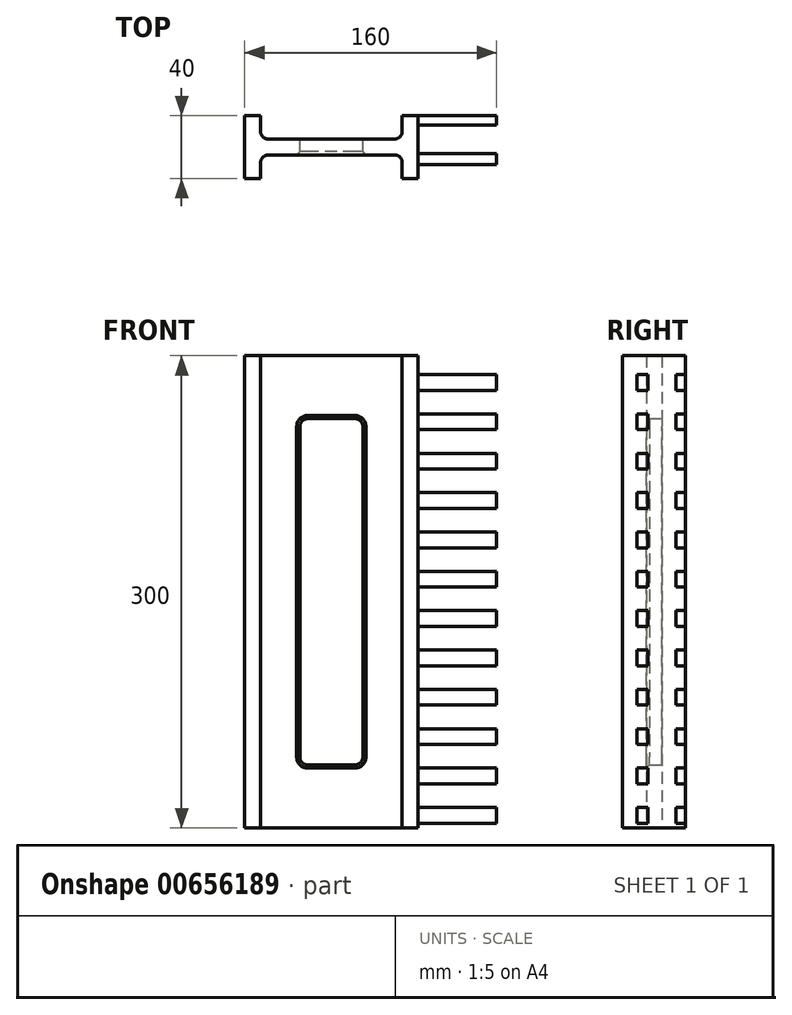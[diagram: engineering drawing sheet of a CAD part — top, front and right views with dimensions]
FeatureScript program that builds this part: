
annotation { "Feature Type Name" : "Feature", "Feature Type Description" : "" }
export const myFeature = defineFeature(function(context is Context, id is Id, definition is map)
    precondition{}
    {
        {
            var Q0;
            Q0=qCreatedBy(makeId("Top.planeOp"),FACE);
            var sketch = newSketch(context, id + "F0", { "sketchPlane" : qUnion([Q0])});
            skLineSegment(sketch, "E0.bottom", {"start": v(0, -5) * mm, "end": v(-40, -5) * mm});
            skLineSegment(sketch, "E0.top", {"start": v(0, 5) * mm, "end": v(-40, 5) * mm});
            skPoint(sketch, "E0.middle", {"position": v(0, 0) * mm});
            skLineSegment(sketch, "E1.bottom", {"start": v(-45, -20) * mm, "end": v(-55, -20) * mm});
            skLineSegment(sketch, "E1.top", {"start": v(-45, 20) * mm, "end": v(-55, 20) * mm});
            skLineSegment(sketch, "E1.left", {"start": v(-45, 10) * mm, "end": v(-45, 20) * mm});
            skLineSegment(sketch, "E1.right", {"start": v(-55, -20) * mm, "end": v(-55, 20) * mm});
            skPoint(sketch, "E1.middle", {"position": v(-50, 0) * mm});
            skPoint(sketch, "E2.orphan", {"position": v(-50, 5) * mm});
            skPoint(sketch, "E0.right.start.orphan", {"position": v(-50, -5) * mm});
            skArc(sketch, "E3.filletArc", {"start": v(-45, 10) * mm, "mid": v(-43.54, 6.46) * mm, "end": v(-40, 5) * mm});
            skLineSegment(sketch, "E4", {"start": v(-45, -20) * mm, "end": v(-45, -10) * mm});
            skPoint(sketch, "E5.visualSharp", {"position": v(-45, -5) * mm});
            skArc(sketch, "E5.filletArc", {"start": v(-40, -5) * mm, "mid": v(-43.54, -6.46) * mm, "end": v(-45, -10) * mm});
            skLineSegment(sketch, "E6", {"start": v(0, 54.25) * mm, "end": v(0, -61.34) * mm, "construction": true});
            skPoint(sketch, "E0.left.end.orphan", {"position": v(50, 5) * mm});
            skPoint(sketch, "E0.left.start.orphan", {"position": v(50, -5) * mm});
            skLineSegment(sketch, "E7.MirrorCS", {"start": v(-45, 30) * mm, "end": v(-45, 20) * mm});
            skLineSegment(sketch, "E8.MirrorCS", {"start": v(0, 5) * mm, "end": v(40, 5) * mm});
            skArc(sketch, "E9.MirrorCS", {"start": v(45, 10) * mm, "mid": v(43.54, 6.46) * mm, "end": v(40, 5) * mm});
            skLineSegment(sketch, "E10.MirrorCS", {"start": v(45, 10) * mm, "end": v(45, 20) * mm});
            skLineSegment(sketch, "E11.MirrorCS", {"start": v(45, 20) * mm, "end": v(55, 20) * mm});
            skLineSegment(sketch, "E12.MirrorCS", {"start": v(55, -20) * mm, "end": v(55, 20) * mm});
            skLineSegment(sketch, "E13.MirrorCS", {"start": v(45, -20) * mm, "end": v(55, -20) * mm});
            skLineSegment(sketch, "E14.MirrorCS", {"start": v(45, -20) * mm, "end": v(45, -10) * mm});
            skArc(sketch, "E15.MirrorCS", {"start": v(40, -5) * mm, "mid": v(43.54, -6.46) * mm, "end": v(45, -10) * mm});
            skLineSegment(sketch, "E16.MirrorCS", {"start": v(0, -5) * mm, "end": v(40, -5) * mm});
            skSolve(sketch);
        }
        {
            var Q0;
            Q0=makeQuery(id+"F0.imprint","IMPRINT",FACE,{"disambiguationData":[TD([[makeQuery(id+"F0.imprint","IMPRINT",EDGE,{"derivedFrom":sQuery(id+"F0.wireOp",EDGE,"E0.bottom")}),-1.0]])]});
            extrude(context, id + "F1", {"entities" : qUnion([Q0]), "depth" : 300 * mm, "offsetDistance" : 25 * mm});
        }
        {
            var Q0;
            Q0=makeQuery(id+"F1.opExtrude","SWEPT_FACE",FACE,{"disambiguationData":[OSD([sQuery(id+"F0.wireOp",EDGE,"E0.top"),sQuery(id+"F0.wireOp",EDGE,"E8.MirrorCS")])]});
            var sketch = newSketch(context, id + "F2", { "sketchPlane" : qUnion([Q0])});
            skLineSegment(sketch, "E17.bottom", {"start": v(-15, 40) * mm, "end": v(15, 40) * mm});
            skLineSegment(sketch, "E17.top", {"start": v(-15, 260) * mm, "end": v(15, 260) * mm});
            skLineSegment(sketch, "E17.left", {"start": v(-20, 45) * mm, "end": v(-20, 255) * mm});
            skLineSegment(sketch, "E17.right", {"start": v(20, 45) * mm, "end": v(20, 255) * mm});
            skPoint(sketch, "E17.middle", {"position": v(0, 150) * mm});
            skPoint(sketch, "E18.visualSharp", {"position": v(20, 260) * mm});
            skArc(sketch, "E18.filletArc", {"start": v(20, 255) * mm, "mid": v(18.54, 258.54) * mm, "end": v(15, 260) * mm});
            skPoint(sketch, "E19.visualSharp", {"position": v(-20, 260) * mm});
            skArc(sketch, "E19.filletArc", {"start": v(-15, 260) * mm, "mid": v(-18.54, 258.54) * mm, "end": v(-20, 255) * mm});
            skPoint(sketch, "E20.visualSharp", {"position": v(20, 40) * mm});
            skArc(sketch, "E20.filletArc", {"start": v(15, 40) * mm, "mid": v(18.54, 41.46) * mm, "end": v(20, 45) * mm});
            skPoint(sketch, "E21.visualSharp", {"position": v(-20, 40) * mm});
            skArc(sketch, "E21.filletArc", {"start": v(-20, 45) * mm, "mid": v(-18.54, 41.46) * mm, "end": v(-15, 40) * mm});
            skSolve(sketch);
        }
        {
            var Q0;
            Q0 = qSketchRegion(id + "F2", true);
            extrude(context, id + "F3", {"entities" : qUnion([Q0]), "operationType" : NewBodyOperationType.REMOVE, "oppositeDirection" : true, "depth" : 25 * mm, "offsetDistance" : 25 * mm});
        }
        {
            var Q0;
            Q0=makeQuery(id+"F3.boolean.opBoolean","INTERSECT",EDGE,{"derivedFrom":[makeQuery(id+"F1.opExtrude","SWEPT_FACE",FACE,{"disambiguationData":[OSD([sQuery(id+"F0.wireOp",EDGE,"E0.bottom"),sQuery(id+"F0.wireOp",EDGE,"E16.MirrorCS")])]}),makeQuery(id+"F3.opExtrude","SWEPT_FACE",FACE,{"disambiguationData":[OSD([sQuery(id+"F2.wireOp",EDGE,"E17.top")])]})]});
            chamfer(context, id + "F4", {"entities" : qUnion([Q0]), "width" : 2 * mm, "tangentPropagation" : true});
        }
        {
            var Q0;
            Q0=makeQuery(id+"F1.opExtrude","SWEPT_FACE",FACE,{"disambiguationData":[OSD([sQuery(id+"F0.wireOp",EDGE,"E12.MirrorCS")])]});
            var sketch = newSketch(context, id + "F5", { "sketchPlane" : qUnion([Q0])});
            skLineSegment(sketch, "E22.bottom", {"start": v(-4, 3) * mm, "end": v(-11, 3) * mm});
            skLineSegment(sketch, "E22.top", {"start": v(-4, 13) * mm, "end": v(-11, 13) * mm});
            skLineSegment(sketch, "E22.left", {"start": v(-4, 3) * mm, "end": v(-4, 13) * mm});
            skPoint(sketch, "E22.middle", {"position": v(-20, 8) * mm});
            skLineSegment(sketch, "E23.0.1.0", {"start": v(-4, 38) * mm, "end": v(-11, 38) * mm});
            skLineSegment(sketch, "E23.0.1.1", {"start": v(-4, 28) * mm, "end": v(-4, 38) * mm});
            skLineSegment(sketch, "E23.0.1.2", {"start": v(-4, 28) * mm, "end": v(-11, 28) * mm});
            skLineSegment(sketch, "E23.0.1.3", {"start": v(-36, 28) * mm, "end": v(-36, 38) * mm});
            skLineSegment(sketch, "E23.0.2.0", {"start": v(-4, 63) * mm, "end": v(-11, 63) * mm});
            skLineSegment(sketch, "E23.0.2.1", {"start": v(-4, 53) * mm, "end": v(-4, 63) * mm});
            skLineSegment(sketch, "E23.0.2.2", {"start": v(-4, 53) * mm, "end": v(-11, 53) * mm});
            skLineSegment(sketch, "E23.0.3.0", {"start": v(-4, 88) * mm, "end": v(-11, 88) * mm});
            skLineSegment(sketch, "E23.0.3.1", {"start": v(-4, 78) * mm, "end": v(-4, 88) * mm});
            skLineSegment(sketch, "E23.0.3.2", {"start": v(-4, 78) * mm, "end": v(-11, 78) * mm});
            skLineSegment(sketch, "E23.0.4.0", {"start": v(-4, 113) * mm, "end": v(-11, 113) * mm});
            skLineSegment(sketch, "E23.0.4.1", {"start": v(-4, 103) * mm, "end": v(-4, 113) * mm});
            skLineSegment(sketch, "E23.0.4.2", {"start": v(-4, 103) * mm, "end": v(-11, 103) * mm});
            skLineSegment(sketch, "E23.0.5.0", {"start": v(-4, 138) * mm, "end": v(-11, 138) * mm});
            skLineSegment(sketch, "E23.0.5.1", {"start": v(-4, 128) * mm, "end": v(-4, 138) * mm});
            skLineSegment(sketch, "E23.0.5.2", {"start": v(-4, 128) * mm, "end": v(-11, 128) * mm});
            skLineSegment(sketch, "E23.0.6.0", {"start": v(-4, 163) * mm, "end": v(-11, 163) * mm});
            skLineSegment(sketch, "E23.0.6.1", {"start": v(-4, 153) * mm, "end": v(-4, 163) * mm});
            skLineSegment(sketch, "E23.0.6.2", {"start": v(-4, 153) * mm, "end": v(-11, 153) * mm});
            skLineSegment(sketch, "E23.0.7.0", {"start": v(-4, 188) * mm, "end": v(-11, 188) * mm});
            skLineSegment(sketch, "E23.0.7.1", {"start": v(-4, 178) * mm, "end": v(-4, 188) * mm});
            skLineSegment(sketch, "E23.0.7.2", {"start": v(-4, 178) * mm, "end": v(-11, 178) * mm});
            skLineSegment(sketch, "E23.0.8.0", {"start": v(-4, 213) * mm, "end": v(-11, 213) * mm});
            skLineSegment(sketch, "E23.0.8.1", {"start": v(-4, 203) * mm, "end": v(-4, 213) * mm});
            skLineSegment(sketch, "E23.0.8.2", {"start": v(-4, 203) * mm, "end": v(-11, 203) * mm});
            skLineSegment(sketch, "E23.0.9.0", {"start": v(-4, 238) * mm, "end": v(-11, 238) * mm});
            skLineSegment(sketch, "E23.0.9.1", {"start": v(-4, 228) * mm, "end": v(-4, 238) * mm});
            skLineSegment(sketch, "E23.0.9.2", {"start": v(-4, 228) * mm, "end": v(-11, 228) * mm});
            skLineSegment(sketch, "E23.0.10.0", {"start": v(-4, 263) * mm, "end": v(-11, 263) * mm});
            skLineSegment(sketch, "E23.0.10.1", {"start": v(-4, 253) * mm, "end": v(-4, 263) * mm});
            skLineSegment(sketch, "E23.0.10.2", {"start": v(-4, 253) * mm, "end": v(-11, 253) * mm});
            skLineSegment(sketch, "E23.0.11.0", {"start": v(-4, 288) * mm, "end": v(-11, 288) * mm});
            skLineSegment(sketch, "E23.0.11.1", {"start": v(-4, 278) * mm, "end": v(-4, 288) * mm});
            skLineSegment(sketch, "E23.0.11.2", {"start": v(-4, 278) * mm, "end": v(-11, 278) * mm});
            skLineSegment(sketch, "E23.1.0.0", {"start": v(21, 13) * mm, "end": v(14, 13) * mm});
            skLineSegment(sketch, "E23.1.0.1", {"start": v(21, 3) * mm, "end": v(21, 13) * mm});
            skLineSegment(sketch, "E23.1.0.2", {"start": v(21, 3) * mm, "end": v(14, 3) * mm});
            skLineSegment(sketch, "E23.1.0.3", {"start": v(-11, 3) * mm, "end": v(-11, 13) * mm});
            skLineSegment(sketch, "E23.1.1.0", {"start": v(21, 38) * mm, "end": v(14, 38) * mm});
            skLineSegment(sketch, "E23.1.1.1", {"start": v(21, 28) * mm, "end": v(21, 38) * mm});
            skLineSegment(sketch, "E23.1.1.2", {"start": v(21, 28) * mm, "end": v(14, 28) * mm});
            skLineSegment(sketch, "E23.1.1.3", {"start": v(-11, 28) * mm, "end": v(-11, 38) * mm});
            skLineSegment(sketch, "E23.1.2.0", {"start": v(21, 63) * mm, "end": v(14, 63) * mm});
            skLineSegment(sketch, "E23.1.2.1", {"start": v(21, 53) * mm, "end": v(21, 63) * mm});
            skLineSegment(sketch, "E23.1.2.2", {"start": v(21, 53) * mm, "end": v(14, 53) * mm});
            skLineSegment(sketch, "E23.1.2.3", {"start": v(-11, 53) * mm, "end": v(-11, 63) * mm});
            skLineSegment(sketch, "E23.1.3.0", {"start": v(21, 88) * mm, "end": v(14, 88) * mm});
            skLineSegment(sketch, "E23.1.3.1", {"start": v(21, 78) * mm, "end": v(21, 88) * mm});
            skLineSegment(sketch, "E23.1.3.2", {"start": v(21, 78) * mm, "end": v(14, 78) * mm});
            skLineSegment(sketch, "E23.1.3.3", {"start": v(-11, 78) * mm, "end": v(-11, 88) * mm});
            skLineSegment(sketch, "E23.1.4.0", {"start": v(21, 113) * mm, "end": v(14, 113) * mm});
            skLineSegment(sketch, "E23.1.4.1", {"start": v(21, 103) * mm, "end": v(21, 113) * mm});
            skLineSegment(sketch, "E23.1.4.2", {"start": v(21, 103) * mm, "end": v(14, 103) * mm});
            skLineSegment(sketch, "E23.1.4.3", {"start": v(-11, 103) * mm, "end": v(-11, 113) * mm});
            skLineSegment(sketch, "E23.1.5.0", {"start": v(21, 138) * mm, "end": v(14, 138) * mm});
            skLineSegment(sketch, "E23.1.5.1", {"start": v(21, 128) * mm, "end": v(21, 138) * mm});
            skLineSegment(sketch, "E23.1.5.2", {"start": v(21, 128) * mm, "end": v(14, 128) * mm});
            skLineSegment(sketch, "E23.1.5.3", {"start": v(-11, 128) * mm, "end": v(-11, 138) * mm});
            skLineSegment(sketch, "E23.1.6.0", {"start": v(21, 163) * mm, "end": v(14, 163) * mm});
            skLineSegment(sketch, "E23.1.6.1", {"start": v(21, 153) * mm, "end": v(21, 163) * mm});
            skLineSegment(sketch, "E23.1.6.2", {"start": v(21, 153) * mm, "end": v(14, 153) * mm});
            skLineSegment(sketch, "E23.1.6.3", {"start": v(-11, 153) * mm, "end": v(-11, 163) * mm});
            skLineSegment(sketch, "E23.1.7.0", {"start": v(21, 188) * mm, "end": v(14, 188) * mm});
            skLineSegment(sketch, "E23.1.7.1", {"start": v(21, 178) * mm, "end": v(21, 188) * mm});
            skLineSegment(sketch, "E23.1.7.2", {"start": v(21, 178) * mm, "end": v(14, 178) * mm});
            skLineSegment(sketch, "E23.1.7.3", {"start": v(-11, 178) * mm, "end": v(-11, 188) * mm});
            skLineSegment(sketch, "E23.1.8.0", {"start": v(21, 213) * mm, "end": v(14, 213) * mm});
            skLineSegment(sketch, "E23.1.8.1", {"start": v(21, 203) * mm, "end": v(21, 213) * mm});
            skLineSegment(sketch, "E23.1.8.2", {"start": v(21, 203) * mm, "end": v(14, 203) * mm});
            skLineSegment(sketch, "E23.1.8.3", {"start": v(-11, 203) * mm, "end": v(-11, 213) * mm});
            skLineSegment(sketch, "E23.1.9.0", {"start": v(21, 238) * mm, "end": v(14, 238) * mm});
            skLineSegment(sketch, "E23.1.9.1", {"start": v(21, 228) * mm, "end": v(21, 238) * mm});
            skLineSegment(sketch, "E23.1.9.2", {"start": v(21, 228) * mm, "end": v(14, 228) * mm});
            skLineSegment(sketch, "E23.1.9.3", {"start": v(-11, 228) * mm, "end": v(-11, 238) * mm});
            skLineSegment(sketch, "E23.1.10.0", {"start": v(21, 263) * mm, "end": v(14, 263) * mm});
            skLineSegment(sketch, "E23.1.10.1", {"start": v(21, 253) * mm, "end": v(21, 263) * mm});
            skLineSegment(sketch, "E23.1.10.2", {"start": v(21, 253) * mm, "end": v(14, 253) * mm});
            skLineSegment(sketch, "E23.1.10.3", {"start": v(-11, 253) * mm, "end": v(-11, 263) * mm});
            skLineSegment(sketch, "E23.1.11.0", {"start": v(21, 288) * mm, "end": v(14, 288) * mm});
            skLineSegment(sketch, "E23.1.11.1", {"start": v(21, 278) * mm, "end": v(21, 288) * mm});
            skLineSegment(sketch, "E23.1.11.2", {"start": v(21, 278) * mm, "end": v(14, 278) * mm});
            skLineSegment(sketch, "E23.1.11.3", {"start": v(-11, 278) * mm, "end": v(-11, 288) * mm});
            skLineSegment(sketch, "E23.2.0.0", {"start": v(21, 13) * mm, "end": v(14, 13) * mm});
            skLineSegment(sketch, "E23.2.0.2", {"start": v(21, 3) * mm, "end": v(14, 3) * mm});
            skLineSegment(sketch, "E23.2.0.3", {"start": v(14, 3) * mm, "end": v(14, 13) * mm});
            skLineSegment(sketch, "E23.2.1.0", {"start": v(21, 38) * mm, "end": v(14, 38) * mm});
            skLineSegment(sketch, "E23.2.1.2", {"start": v(21, 28) * mm, "end": v(14, 28) * mm});
            skLineSegment(sketch, "E23.2.1.3", {"start": v(14, 28) * mm, "end": v(14, 38) * mm});
            skLineSegment(sketch, "E23.2.2.0", {"start": v(21, 63) * mm, "end": v(14, 63) * mm});
            skLineSegment(sketch, "E23.2.2.2", {"start": v(21, 53) * mm, "end": v(14, 53) * mm});
            skLineSegment(sketch, "E23.2.2.3", {"start": v(14, 53) * mm, "end": v(14, 63) * mm});
            skLineSegment(sketch, "E23.2.3.0", {"start": v(21, 88) * mm, "end": v(14, 88) * mm});
            skLineSegment(sketch, "E23.2.3.2", {"start": v(21, 78) * mm, "end": v(14, 78) * mm});
            skLineSegment(sketch, "E23.2.3.3", {"start": v(14, 78) * mm, "end": v(14, 88) * mm});
            skLineSegment(sketch, "E23.2.4.0", {"start": v(21, 113) * mm, "end": v(14, 113) * mm});
            skLineSegment(sketch, "E23.2.4.2", {"start": v(21, 103) * mm, "end": v(14, 103) * mm});
            skLineSegment(sketch, "E23.2.4.3", {"start": v(14, 103) * mm, "end": v(14, 113) * mm});
            skLineSegment(sketch, "E23.2.5.0", {"start": v(21, 138) * mm, "end": v(14, 138) * mm});
            skLineSegment(sketch, "E23.2.5.2", {"start": v(21, 128) * mm, "end": v(14, 128) * mm});
            skLineSegment(sketch, "E23.2.5.3", {"start": v(14, 128) * mm, "end": v(14, 138) * mm});
            skLineSegment(sketch, "E23.2.6.0", {"start": v(21, 163) * mm, "end": v(14, 163) * mm});
            skLineSegment(sketch, "E23.2.6.2", {"start": v(21, 153) * mm, "end": v(14, 153) * mm});
            skLineSegment(sketch, "E23.2.6.3", {"start": v(14, 153) * mm, "end": v(14, 163) * mm});
            skLineSegment(sketch, "E23.2.7.0", {"start": v(21, 188) * mm, "end": v(14, 188) * mm});
            skLineSegment(sketch, "E23.2.7.2", {"start": v(21, 178) * mm, "end": v(14, 178) * mm});
            skLineSegment(sketch, "E23.2.7.3", {"start": v(14, 178) * mm, "end": v(14, 188) * mm});
            skLineSegment(sketch, "E23.2.8.0", {"start": v(21, 213) * mm, "end": v(14, 213) * mm});
            skLineSegment(sketch, "E23.2.8.2", {"start": v(21, 203) * mm, "end": v(14, 203) * mm});
            skLineSegment(sketch, "E23.2.8.3", {"start": v(14, 203) * mm, "end": v(14, 213) * mm});
            skLineSegment(sketch, "E23.2.9.0", {"start": v(21, 238) * mm, "end": v(14, 238) * mm});
            skLineSegment(sketch, "E23.2.9.2", {"start": v(21, 228) * mm, "end": v(14, 228) * mm});
            skLineSegment(sketch, "E23.2.9.3", {"start": v(14, 228) * mm, "end": v(14, 238) * mm});
            skLineSegment(sketch, "E23.2.10.0", {"start": v(21, 263) * mm, "end": v(14, 263) * mm});
            skLineSegment(sketch, "E23.2.10.2", {"start": v(21, 253) * mm, "end": v(14, 253) * mm});
            skLineSegment(sketch, "E23.2.10.3", {"start": v(14, 253) * mm, "end": v(14, 263) * mm});
            skLineSegment(sketch, "E23.2.11.0", {"start": v(21, 288) * mm, "end": v(14, 288) * mm});
            skLineSegment(sketch, "E23.2.11.2", {"start": v(21, 278) * mm, "end": v(14, 278) * mm});
            skLineSegment(sketch, "E23.2.11.3", {"start": v(14, 278) * mm, "end": v(14, 288) * mm});
            skLineSegment(sketch, "E23.direction2", {"start": v(-36, 13) * mm, "end": v(-36, 38) * mm, "construction": true});
            skPoint(sketch, "E24.orphan", {"position": v(46, 278) * mm});
            skPoint(sketch, "E25.orphan", {"position": v(46, 263) * mm});
            skPoint(sketch, "E26.orphan", {"position": v(46, 253) * mm});
            skPoint(sketch, "E27.orphan", {"position": v(46, 238) * mm});
            skPoint(sketch, "E28.orphan", {"position": v(46, 228) * mm});
            skPoint(sketch, "E29.orphan", {"position": v(46, 203) * mm});
            skPoint(sketch, "E30.orphan", {"position": v(46, 178) * mm});
            skPoint(sketch, "E31.orphan", {"position": v(46, 188) * mm});
            skPoint(sketch, "E32.orphan", {"position": v(46, 153) * mm});
            skPoint(sketch, "E33.orphan", {"position": v(46, 128) * mm});
            skPoint(sketch, "E34.orphan", {"position": v(46, 103) * mm});
            skPoint(sketch, "E35.orphan", {"position": v(46, 78) * mm});
            skPoint(sketch, "E36.orphan", {"position": v(46, 53) * mm});
            skPoint(sketch, "E37.orphan", {"position": v(46, 28) * mm});
            skPoint(sketch, "E22.right.start.orphan", {"position": v(-36, 3) * mm});
            skSolve(sketch);
        }
        {
            var Q0;
            Q0=makeQuery(id+"F5.imprint","IMPRINT",FACE,{"disambiguationData":[TD([[makeQuery(id+"F5.imprint","IMPRINT",EDGE,{"derivedFrom":sQuery(id+"F5.wireOp",EDGE,"E23.0.11.1")}),1.0]])]});
            var Q1;
            {var subQ0=sQuery(id+"F5.wireOp",EDGE,"E23.2.11.3");Q1=makeQuery(id+"F5.imprint","IMPRINT",FACE,{"disambiguationData":[TD([[makeQuery(id+"F5.imprint","IMPRINT",EDGE,{"derivedFrom":subQ0}),-1.0]])]});}
            var Q2;
            Q2=makeQuery(id+"F5.imprint","IMPRINT",FACE,{"disambiguationData":[TD([[makeQuery(id+"F5.imprint","IMPRINT",EDGE,{"derivedFrom":sQuery(id+"F5.wireOp",EDGE,"E23.0.10.1")}),1.0]])]});
            var Q3;
            {var subQ0=sQuery(id+"F5.wireOp",EDGE,"E23.2.10.3");Q3=makeQuery(id+"F5.imprint","IMPRINT",FACE,{"disambiguationData":[TD([[makeQuery(id+"F5.imprint","IMPRINT",EDGE,{"derivedFrom":subQ0}),-1.0]])]});}
            var Q4;
            Q4=makeQuery(id+"F5.imprint","IMPRINT",FACE,{"disambiguationData":[TD([[makeQuery(id+"F5.imprint","IMPRINT",EDGE,{"derivedFrom":sQuery(id+"F5.wireOp",EDGE,"E23.0.9.1")}),1.0]])]});
            var Q5;
            {var subQ0=sQuery(id+"F5.wireOp",EDGE,"E23.2.9.3");Q5=makeQuery(id+"F5.imprint","IMPRINT",FACE,{"disambiguationData":[TD([[makeQuery(id+"F5.imprint","IMPRINT",EDGE,{"derivedFrom":subQ0}),-1.0]])]});}
            var Q6;
            Q6=makeQuery(id+"F5.imprint","IMPRINT",FACE,{"disambiguationData":[TD([[makeQuery(id+"F5.imprint","IMPRINT",EDGE,{"derivedFrom":sQuery(id+"F5.wireOp",EDGE,"E23.0.8.1")}),1.0]])]});
            var Q7;
            {var subQ0=sQuery(id+"F5.wireOp",EDGE,"E23.2.8.3");Q7=makeQuery(id+"F5.imprint","IMPRINT",FACE,{"disambiguationData":[TD([[makeQuery(id+"F5.imprint","IMPRINT",EDGE,{"derivedFrom":subQ0}),-1.0]])]});}
            var Q8;
            Q8=makeQuery(id+"F5.imprint","IMPRINT",FACE,{"disambiguationData":[TD([[makeQuery(id+"F5.imprint","IMPRINT",EDGE,{"derivedFrom":sQuery(id+"F5.wireOp",EDGE,"E23.0.7.1")}),1.0]])]});
            var Q9;
            {var subQ0=sQuery(id+"F5.wireOp",EDGE,"E23.2.7.3");Q9=makeQuery(id+"F5.imprint","IMPRINT",FACE,{"disambiguationData":[TD([[makeQuery(id+"F5.imprint","IMPRINT",EDGE,{"derivedFrom":subQ0}),-1.0]])]});}
            var Q10;
            Q10=makeQuery(id+"F5.imprint","IMPRINT",FACE,{"disambiguationData":[TD([[makeQuery(id+"F5.imprint","IMPRINT",EDGE,{"derivedFrom":sQuery(id+"F5.wireOp",EDGE,"E23.0.6.1")}),1.0]])]});
            var Q11;
            {var subQ0=sQuery(id+"F5.wireOp",EDGE,"E23.2.6.3");Q11=makeQuery(id+"F5.imprint","IMPRINT",FACE,{"disambiguationData":[TD([[makeQuery(id+"F5.imprint","IMPRINT",EDGE,{"derivedFrom":subQ0}),-1.0]])]});}
            var Q12;
            Q12=makeQuery(id+"F5.imprint","IMPRINT",FACE,{"disambiguationData":[TD([[makeQuery(id+"F5.imprint","IMPRINT",EDGE,{"derivedFrom":sQuery(id+"F5.wireOp",EDGE,"E23.0.5.1")}),1.0]])]});
            var Q13;
            {var subQ0=sQuery(id+"F5.wireOp",EDGE,"E23.2.5.3");Q13=makeQuery(id+"F5.imprint","IMPRINT",FACE,{"disambiguationData":[TD([[makeQuery(id+"F5.imprint","IMPRINT",EDGE,{"derivedFrom":subQ0}),-1.0]])]});}
            var Q14;
            Q14=makeQuery(id+"F5.imprint","IMPRINT",FACE,{"disambiguationData":[TD([[makeQuery(id+"F5.imprint","IMPRINT",EDGE,{"derivedFrom":sQuery(id+"F5.wireOp",EDGE,"E23.0.4.1")}),1.0]])]});
            var Q15;
            {var subQ0=sQuery(id+"F5.wireOp",EDGE,"E23.2.4.3");Q15=makeQuery(id+"F5.imprint","IMPRINT",FACE,{"disambiguationData":[TD([[makeQuery(id+"F5.imprint","IMPRINT",EDGE,{"derivedFrom":subQ0}),-1.0]])]});}
            var Q16;
            Q16=makeQuery(id+"F5.imprint","IMPRINT",FACE,{"disambiguationData":[TD([[makeQuery(id+"F5.imprint","IMPRINT",EDGE,{"derivedFrom":sQuery(id+"F5.wireOp",EDGE,"E23.0.3.1")}),1.0]])]});
            var Q17;
            {var subQ0=sQuery(id+"F5.wireOp",EDGE,"E23.2.3.3");Q17=makeQuery(id+"F5.imprint","IMPRINT",FACE,{"disambiguationData":[TD([[makeQuery(id+"F5.imprint","IMPRINT",EDGE,{"derivedFrom":subQ0}),-1.0]])]});}
            var Q18;
            Q18=makeQuery(id+"F5.imprint","IMPRINT",FACE,{"disambiguationData":[TD([[makeQuery(id+"F5.imprint","IMPRINT",EDGE,{"derivedFrom":sQuery(id+"F5.wireOp",EDGE,"E23.0.2.1")}),1.0]])]});
            var Q19;
            {var subQ0=sQuery(id+"F5.wireOp",EDGE,"E23.2.2.3");Q19=makeQuery(id+"F5.imprint","IMPRINT",FACE,{"disambiguationData":[TD([[makeQuery(id+"F5.imprint","IMPRINT",EDGE,{"derivedFrom":subQ0}),-1.0]])]});}
            var Q20;
            Q20=makeQuery(id+"F5.imprint","IMPRINT",FACE,{"disambiguationData":[TD([[makeQuery(id+"F5.imprint","IMPRINT",EDGE,{"derivedFrom":sQuery(id+"F5.wireOp",EDGE,"E23.0.1.1")}),1.0]])]});
            var Q21;
            {var subQ0=sQuery(id+"F5.wireOp",EDGE,"E23.2.1.3");Q21=makeQuery(id+"F5.imprint","IMPRINT",FACE,{"disambiguationData":[TD([[makeQuery(id+"F5.imprint","IMPRINT",EDGE,{"derivedFrom":subQ0}),-1.0]])]});}
            var Q22;
            Q22=makeQuery(id+"F5.imprint","IMPRINT",FACE,{"disambiguationData":[TD([[makeQuery(id+"F5.imprint","IMPRINT",EDGE,{"derivedFrom":sQuery(id+"F5.wireOp",EDGE,"E22.left")}),1.0]])]});
            var Q23;
            {var subQ0=sQuery(id+"F5.wireOp",EDGE,"E23.2.0.3");Q23=makeQuery(id+"F5.imprint","IMPRINT",FACE,{"disambiguationData":[TD([[makeQuery(id+"F5.imprint","IMPRINT",EDGE,{"derivedFrom":subQ0}),-1.0]])]});}
            extrude(context, id + "F6", {"entities" : qUnion([Q0, Q1, Q2, Q3, Q4, Q5, Q6, Q7, Q8, Q9, Q10, Q11, Q12, Q13, Q14, Q15, Q16, Q17, Q18, Q19, Q20, Q21, Q22, Q23]), "operationType" : NewBodyOperationType.ADD, "depth" : 50 * mm, "offsetDistance" : 25 * mm});
        }
    });
